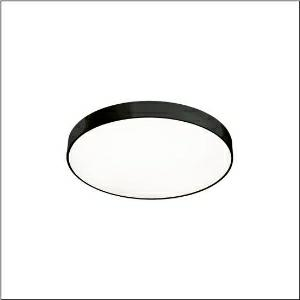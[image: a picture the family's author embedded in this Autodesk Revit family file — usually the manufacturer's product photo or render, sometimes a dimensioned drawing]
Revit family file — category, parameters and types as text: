
# Revit family: round_21_m_51mr36fm8421b
name_source: partatom
category: Lighting Fixtures
units: mm (PartAtom-declared; Revit-internal decimal feet)

## family parameters
Cut with Voids When Loaded = No
Host = Face
Light Source = No
Part Type = Normal
Room Calculation Point = No
Round Connector Dimension = Use Diameter
Shared = No

## types (1)
- --- (1 x LED, 8900 lm, 62.6 W, 4000K)
    Apparent Load = 63 VA
    CIE Flux Codes = 49 80 96 100 100
    Color Rendering = 80
    Color Temperature = 4000K
    Default Elevation = 1800 mm
    Description = Round 21 M, wall and ceiling luminaire, primary optical cover: cover, of PMMA, opal, light emission: direct distribution, primary light characteristic: symmetric, installation type: surface-mounted, suspended mounting, LED, rated luminous flux: 8.140lm, luminous efficacy: 133lm/W, light colour: 840, colour temperature: 4000K, control gear: ON/OFF Multilumen, with terminal, 3-pole, mains connection: 230V, AC, 50/60Hz, rated input power: 61W, housing, of aluminium, coated, black, diameter: 600mm, height: 62mm, protection rating (complete): IP40, insulation class (complete): insulation class I (protective earthing), certification: CE, impact resistance: IK04, permissible operating ambient temperature: -10..+35°C, packaging unit: 1 piece
    Height = 87 mm
    Lamp = 1 x LED
    Lamp Light Flux = 8900 lm
    Lamp Power = 62.6 W
    Lamp count = 1
    Length = 600 mm
    Luminous efficacy = 142 lm/W
    Manufacturer = Siteco
    ModVariant = No
    Model = 51MR36FM8421B
    Mounting Place = Ceiling
    Mounting Type = Surface mounted
    Number of Poles = 1
    OnlyDefault = Yes
    Power Factor = 1
    Product Name = Round 21 M
    Product group = wall and ceiling luminaire | ceiling mounted
    ProductGroupID = 304
    Protection Class = Protection class I
    Protection Degree = IP 40
    RLX_Detail_Level = 1
    RLX_Emergency_Light_Flux = 0 lm
    RLX_Emergency_Type = 0
    RLX_Emergency_Type_DB = No
    RlxData = <blob elided: 20417 chars, md5=b921a071>
    Socket = socket
    Standby Power = 0 W
    System Light Flux = 8900 lm
    System Power = 63 W
    Type Comments = factory setting: luminous flux: 100 % | (ON | ON | ON | ON) | 700 mA
    Type Image = l_1258332.jpg
    URL = http://relux.com
    VarID = @adj_039481
    Voltage = 0 V
    Weight = 0.00 kg
    Width = 0 mm  [stored 0 ft]

note: [stored X ft] marks values corroborated as IEEE doubles in the binary element streams (Revit-internal decimal feet)

## geometry (parser evidence)
native form markers: Blend x4, Sweep x9
no freeform markers — native parametric forms only
